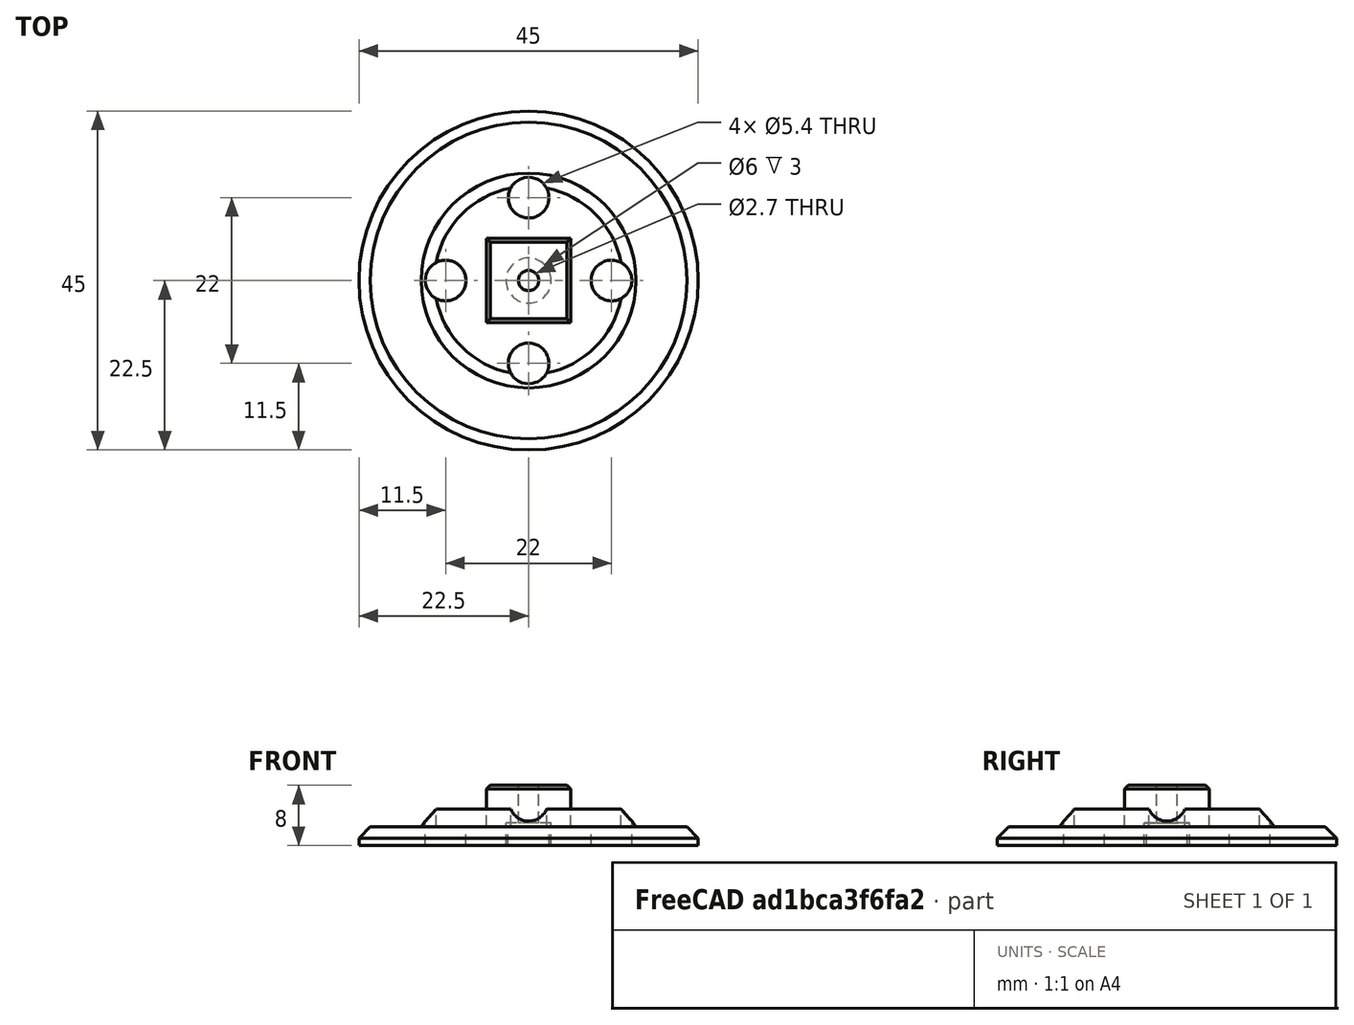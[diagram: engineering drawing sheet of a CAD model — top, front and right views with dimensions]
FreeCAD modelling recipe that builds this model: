
FCSTD DOCUMENT  (FreeCAD 0.14R2935 (Git))
Label: tendon_wheel_mx_12_23_mm_top
License: CC-BY 3.0
LicenseURL: http://creativecommons.org/licenses/by/3.0/
objects: Part::Cylinder×8, Part::MultiFuse×4, Part::Cut×3, Part::Chamfer×2, Part::Cone×1, Part::Box×1
note: 19 computed .brp shape members not serialized (recipe doc carries the construction recipe); baked Part::Feature solids carry a one-line shape summary decoded from their .brp

FEATURE [Part::Cylinder] Cylinder
  Angle = 360
  Height = 6
  Placement = pos=(0,0,2) rot=(0,0,1;0rad)
  Radius = 12.5
FEATURE [Part::Cylinder] Cylinder001
  Angle = 360
  Height = 2.5
  Placement = pos=(0,0,-0.5) rot=(0,0,1;0rad)
  Radius = 22.5
FEATURE [Part::Cone] Cone
  Angle = 360
  Height = 4
  Placement = pos=(0,0,1) rot=(0,0,1;0rad)
  Radius1 = 15
  Radius2 = 12
FEATURE [Part::Box] Box  label="Cube"
  Height = 5.5
  Length = 11.2
  Placement = pos=(-5.6,-5.6,2) rot=(0,0,1;0rad)
  Width = 11.2
FEATURE [Part::MultiFuse] Fusion
  Shapes = -> [Cone,Cylinder001]
FEATURE [Part::Cylinder] Cylinder002  label="Cylinder004"
  Angle = 360
  Height = 20
  Placement = pos=(0,0,-5) rot=(0,0,1;0rad)
  Radius = 1.35
FEATURE [Part::Cut] Cut
  Base = -> Fusion
  Tool = -> Cylinder
FEATURE [Part::MultiFuse] Fusion001
  Shapes = -> [Cut,Box]
FEATURE [Part::Cylinder] Cylinder003  label="Cylinder012"
  Angle = 360
  Height = 3
  Placement = pos=(0,0,-0.5) rot=(0,0,1;0rad)
  Radius = 3
FEATURE [Part::MultiFuse] Fusion002
  Shapes = -> [Cylinder003,Cylinder002]
FEATURE [Part::Cut] Cut001
  Base = -> Fusion001
  Tool = -> Fusion002
FEATURE [Part::Chamfer] Chamfer
  Base = -> Cut001
  Edges = 4 edges r=0.5: [Edge1,Edge2,Edge3,Edge4]
FEATURE [Part::Cylinder] Cylinder005  label="TopHole005"
  Angle = 360
  Height = 20
  Placement = pos=(11,0,-5) rot=(0,0,1;0rad)
  Radius = 2.7
FEATURE [Part::Cylinder] Cylinder008  label="TopHole006"
  Angle = 360
  Height = 20
  Placement = pos=(0,11,-5) rot=(0,0,1;0rad)
  Radius = 2.7
FEATURE [Part::Cylinder] Cylinder009  label="TopHole004"
  Angle = 360
  Height = 20
  Placement = pos=(-11,0,-5) rot=(0,0,1;0rad)
  Radius = 2.7
FEATURE [Part::Cylinder] Cylinder011  label="TopHole007"
  Angle = 360
  Height = 20
  Placement = pos=(0,-11,-5) rot=(0,0,1;0rad)
  Radius = 2.7
FEATURE [Part::MultiFuse] Fusion003
  Shapes = -> [Cylinder011,Cylinder008,Cylinder009,Cylinder005]
FEATURE [Part::Cut] Cut002
  Base = -> Chamfer
  Tool = -> Fusion003
FEATURE [Part::Chamfer] Chamfer001
  Base = -> Cut002
  Edges = 1 edges r=1.5: [Edge66]
